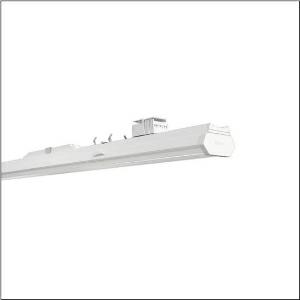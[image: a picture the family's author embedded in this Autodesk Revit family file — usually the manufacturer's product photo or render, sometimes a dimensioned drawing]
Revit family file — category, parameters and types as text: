
# Revit family: licross_r__11_protected_mo_51tp117n485g_c591
name_source: partatom
category: Lighting Fixtures
units: mm (PartAtom-declared; Revit-internal decimal feet)

## family parameters
Cut with Voids When Loaded = No
Host = Face
Light Source = No
Part Type = Normal
Room Calculation Point = No
Round Connector Dimension = Use Diameter
Shared = No

## types (1)
- Licross® 11 Protected MO (1 x LED, 8680 lm, 48.6 W, 4000K)
    Apparent Load = 49 VA
    CIE Flux Codes = 83 94 98 100 100
    Color Rendering = 80
    Color Temperature = 4000K
    Default Elevation = 1800 mm
    Description = Licross® 11 Protected MO, luminaire insert, of sheet steel, galvanised, coil coated, white, length: 1.500mm, width: 90mm, height: 101mm, LED rated luminous flux: 8.680lm, light colour: 840, control gear: ON/OFF, control gear: ECG, with plug, 3-pole, with phase selection, mains connection: 220..240V, AC, 50/60Hz, halogen-free wiring, primary light control with lens, of plastic, primary optical cover: cover, of PMMA, light emission: direct with ceiling illumination distribution, primary light characteristic: symmetric, protection rating (complete): IP64, insulation class (complete): insulation class I (protective earthing), certification: CE, ENEC, VDE, UKCA, protection symbol: D if used in an environment with conductive dust loads with corresponding accessories, impact resistance: IK06, corresponds to IFS (International Featured Standards) requirements for safety and quality in the food industry, reducing of maximum allowable ambient temperature of 5°C with ceiling mounting, LABS conformity tested according to VDMA 24364:2018-05, packaging unit: 1 piece
    Height = 92 mm
    Lamp = 1 x LED
    Lamp Light Flux = 8680 lm
    Lamp Power = 48.6 W
    Lamp count = 1
    Length = 1500 mm
    Luminous efficacy = 179 lm/W
    Manufacturer = Siteco
    ModVariant = No
    Model = 51TP117N485G
    Mounting Place = Ceiling
    Mounting Type = Pendant
    Number of Poles = 1
    OnlyDefault = Yes
    Power Factor = 1
    Product Name = Licross® 11 Protected MO
    Product group = luminaire insert
    ProductGroupID = 902
    Protection Class = Protection class I
    Protection Degree = IP 64
    RLX_Detail_Level = 1
    RlxData = <blob elided: 20325 chars, md5=7c9a776d>
    Socket = socket
    Standby Power = 0 W
    System Light Flux = 8680 lm
    System Power = 49 W
    Type Comments = Product without accessories
    Type Image = l_1256148.jpg
    URL = http://relux.com
    VarID = ---
    Voltage = 0 V
    Weight = 0.00 kg
    Width = 88 mm

## geometry (parser evidence)
native form markers: Blend x4, Sweep x11
no freeform markers — native parametric forms only
